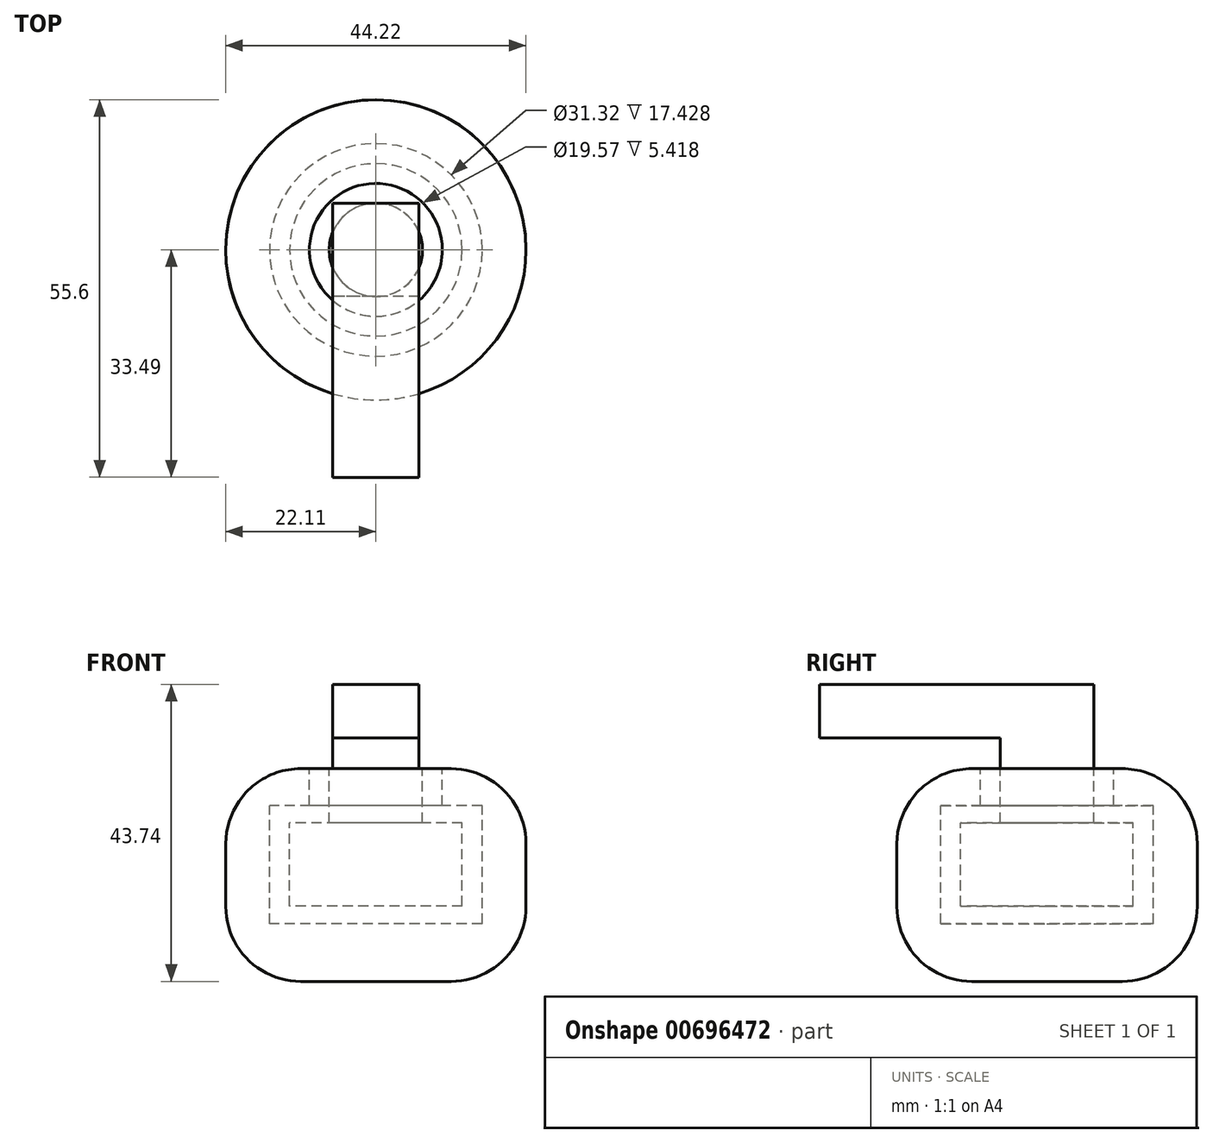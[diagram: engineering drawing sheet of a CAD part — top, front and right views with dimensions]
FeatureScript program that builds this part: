
annotation { "Feature Type Name" : "Feature", "Feature Type Description" : "" }
export const myFeature = defineFeature(function(context is Context, id is Id, definition is map)
    precondition{}
    {
        {
            var Q0;
            Q0=qCreatedBy(makeId("Right.planeOp"),FACE);
            var sketch = newSketch(context, id + "F0", { "sketchPlane" : qUnion([Q0])});
            skLineSegment(sketch, "E0.bottom", {"start": v(38.1, 40.36) * mm, "end": v(-38.1, 40.36) * mm});
            skLineSegment(sketch, "E0.left", {"start": v(38.1, 40.36) * mm, "end": v(38.1, 9.04) * mm});
            skLineSegment(sketch, "E0.right", {"start": v(-38.1, 40.36) * mm, "end": v(-38.1, 9.04) * mm});
            skPoint(sketch, "E0.middle", {"position": v(0, 0) * mm});
            skLineSegment(sketch, "E1.top", {"start": v(12.7, 80.73) * mm, "end": v(-12.7, 80.73) * mm});
            skLineSegment(sketch, "E1.left", {"start": v(12.7, 9.04) * mm, "end": v(12.7, 80.73) * mm});
            skLineSegment(sketch, "E1.right", {"start": v(-12.7, 9.04) * mm, "end": v(-12.7, 80.73) * mm});
            skPoint(sketch, "E1.middle", {"position": v(0, 40.36) * mm});
            skLineSegment(sketch, "E2", {"start": v(-12.7, 32.41) * mm, "end": v(-6.87, 32.41) * mm});
            skLineSegment(sketch, "E3", {"start": v(-6.87, 32.41) * mm, "end": v(-6.87, 40.36) * mm});
            skLineSegment(sketch, "E4", {"start": v(0, 40.36) * mm, "end": v(0, 9.04) * mm});
            skLineSegment(sketch, "E5.MirrorCS", {"start": v(6.87, 32.41) * mm, "end": v(6.87, 40.36) * mm});
            skLineSegment(sketch, "E6.MirrorCS", {"start": v(12.7, 32.41) * mm, "end": v(6.87, 32.41) * mm});
            skLineSegment(sketch, "E7", {"start": v(-12.7, 20.12) * mm, "end": v(12.7, 20.12) * mm});
            skLineSegment(sketch, "E8", {"start": v(-38.1, 9.04) * mm, "end": v(38.1, 9.04) * mm});
            skPoint(sketch, "E9.orphan", {"position": v(-12.7, 0) * mm});
            skPoint(sketch, "E10.orphan", {"position": v(12.7, 0) * mm});
            skPoint(sketch, "E11.orphan", {"position": v(38.1, -40.36) * mm});
            skPoint(sketch, "E12.orphan", {"position": v(-38.1, -40.36) * mm});
            skPoint(sketch, "E13.orphan", {"position": v(0, -40.36) * mm});
            skLineSegment(sketch, "E14", {"start": v(-9.78, 40.36) * mm, "end": v(-9.78, 34.95) * mm});
            skLineSegment(sketch, "E15", {"start": v(-9.78, 34.95) * mm, "end": v(-15.66, 34.95) * mm});
            skLineSegment(sketch, "E16", {"start": v(-15.66, 34.95) * mm, "end": v(-15.66, 17.52) * mm});
            skLineSegment(sketch, "E17", {"start": v(-15.66, 17.52) * mm, "end": v(0, 17.52) * mm});
            skLineSegment(sketch, "E18", {"start": v(-6.87, 40.36) * mm, "end": v(-6.87, 44.88) * mm});
            skPoint(sketch, "E18.endSnap0", {"position": v(-12.7, 44.88) * mm});
            skLineSegment(sketch, "E19", {"start": v(-6.87, 44.88) * mm, "end": v(-33.5, 44.88) * mm});
            skLineSegment(sketch, "E20", {"start": v(-33.5, 44.88) * mm, "end": v(-33.5, 52.78) * mm});
            skLineSegment(sketch, "E21", {"start": v(-33.5, 52.78) * mm, "end": v(6.87, 52.78) * mm});
            skLineSegment(sketch, "E22", {"start": v(6.87, 52.78) * mm, "end": v(6.87, 40.36) * mm});
            skLineSegment(sketch, "E23", {"start": v(-22.1, 40.36) * mm, "end": v(-22.1, 9.04) * mm});
            skSolve(sketch);
        }
        {
            var Q0;
            {var subQ0=sQuery(id+"F0.wireOp",EDGE,"E8");var subQ1=sQuery(id+"F0.wireOp",EDGE,"E1.right");var subQ2=makeQuery(id+"F0.imprint","INTERSECT",VERTEX,{"derivedFrom":[subQ1,subQ0]});Q0=makeQuery(id+"F0.imprint","IMPRINT",FACE,{"disambiguationData":[TD([[makeQuery(id+"F0.imprint","IMPRINT",EDGE,{"disambiguationData":[TD([[subQ2,-1.0]])],"derivedFrom":subQ1}),-1.0]])]});}
            var Q1;
            {var subQ0=sQuery(id+"F0.wireOp",EDGE,"E2");Q1=makeQuery(id+"F0.imprint","IMPRINT",FACE,{"disambiguationData":[TD([[makeQuery(id+"F0.imprint","IMPRINT",EDGE,{"derivedFrom":subQ0}),-1.0]])]});}
            var Q2;
            {var subQ0=sQuery(id+"F0.wireOp",EDGE,"E14");Q2=makeQuery(id+"F0.imprint","IMPRINT",FACE,{"disambiguationData":[TD([[makeQuery(id+"F0.imprint","IMPRINT",EDGE,{"derivedFrom":subQ0}),-1.0]])]});}
            var Q3;
            {var subQ9=sQuery(id+"F0.wireOp",EDGE,"E16");Q3=makeQuery(id+"F0.imprint","IMPRINT",FACE,{"disambiguationData":[TD([[makeQuery(id+"F0.imprint","IMPRINT",EDGE,{"derivedFrom":subQ9}),-1.0]])]});}
            var Q4;
            Q4=sQuery(id+"F0.wireOp",EDGE,"E4");
            revolve(context, id + "F1", {"surfaceOperationType" : NewSurfaceOperationType.NEW, "entities" : qUnion([Q0, Q1, Q2, Q3]), "axis" : qUnion([Q4]), "revolveType" : RevolveType.FULL});
        }
        {
            var Q0;
            {var subQ0=sQuery(id+"F0.wireOp",EDGE,"E18");Q0=makeQuery(id+"F0.imprint","IMPRINT",FACE,{"disambiguationData":[TD([[makeQuery(id+"F0.imprint","IMPRINT",EDGE,{"derivedFrom":subQ0}),-1.0]])]});}
            var Q1;
            {var subQ5=sQuery(id+"F0.wireOp",EDGE,"E20");Q1=makeQuery(id+"F0.imprint","IMPRINT",FACE,{"disambiguationData":[TD([[makeQuery(id+"F0.imprint","IMPRINT",EDGE,{"derivedFrom":subQ5}),-1.0]])]});}
            extrude(context, id + "F2", {"entities" : qUnion([Q0, Q1]), "operationType" : NewBodyOperationType.ADD, "endBound" : BoundingType.SYMMETRIC, "depth" : 12.7 * mm, "offsetDistance" : 25.4 * mm});
        }
        {
            var Q0;
            Q0=makeQuery(id+"F1.opRevolve","SWEPT_EDGE",EDGE,{"disambiguationData":[OSD([sQuery(id+"F0.wireOp",EDGE,"E8"),sQuery(id+"F0.wireOp",EDGE,"E23")])]});
            var Q1;
            Q1=makeQuery(id+"F1.opRevolve","SWEPT_EDGE",EDGE,{"disambiguationData":[OSD([sQuery(id+"F0.wireOp",EDGE,"E0.bottom"),sQuery(id+"F0.wireOp",EDGE,"E23")])]});
            fillet(context, id + "F3", {"entities" : qUnion([Q0, Q1]), "radius" : 11.04 * mm, "tangentPropagation" : true, "allowEdgeOverflow" : false});
        }
    });
